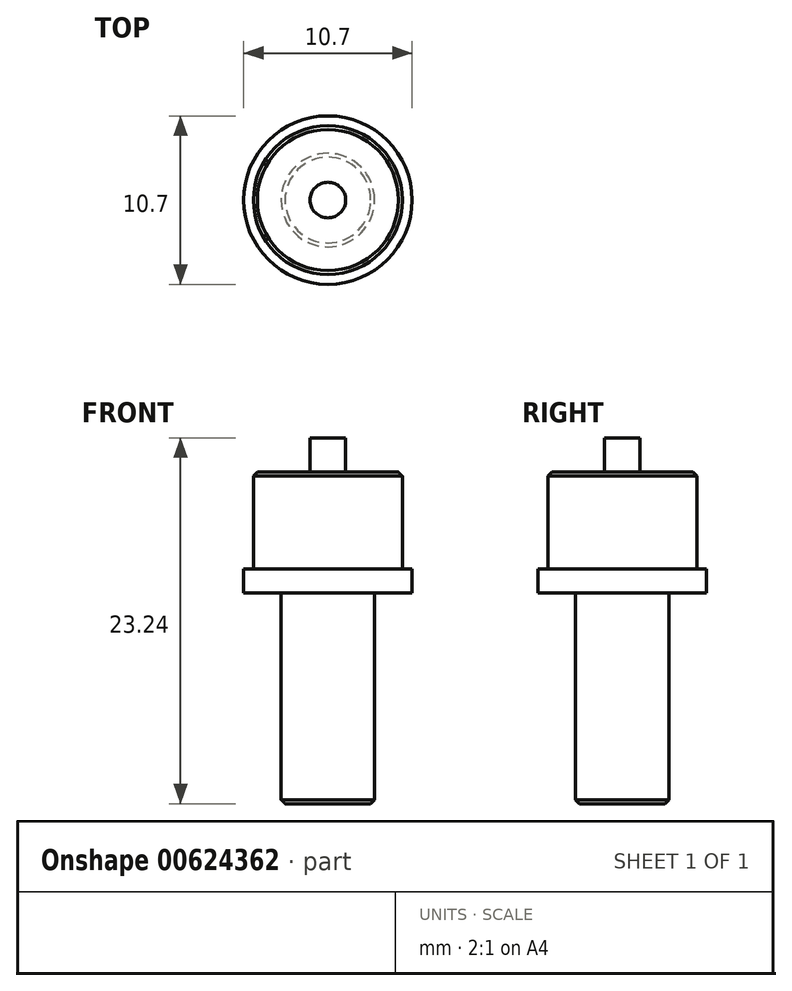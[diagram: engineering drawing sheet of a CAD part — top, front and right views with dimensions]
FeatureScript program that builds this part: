
annotation { "Feature Type Name" : "Feature", "Feature Type Description" : "" }
export const myFeature = defineFeature(function(context is Context, id is Id, definition is map)
    precondition{}
    {
        {
            var Q0;
            Q0=qCreatedBy(makeId("Top.planeOp"),FACE);
            var sketch = newSketch(context, id + "F0", { "sketchPlane" : qUnion([Q0])});
            skCircle(sketch, "E0", {"center": v(0, 0) * mm, "radius": 5.35 * mm});
            skSolve(sketch);
        }
        {
            var Q0;
            Q0=makeQuery(id+"F0.imprint","IMPRINT",FACE,{"disambiguationData":[TD([[makeQuery(id+"F0.imprint","IMPRINT",EDGE,{"derivedFrom":sQuery(id+"F0.wireOp",EDGE,"E0")}),1.0]])]});
            extrude(context, id + "F1", {"entities" : qUnion([Q0]), "depth" : 1.5 * mm, "offsetDistance" : 25 * mm});
        }
        {
            var Q0;
            Q0=makeQuery(id+"F1.opExtrude","CAP_FACE",FACE,{"disambiguationData":[OSD([sQuery(id+"F0.wireOp",EDGE,"E0")])],"isStart":false});
            var sketch = newSketch(context, id + "F2", { "sketchPlane" : qUnion([Q0])});
            skCircle(sketch, "E1", {"center": v(0, 0) * mm, "radius": 4.73 * mm});
            skSolve(sketch);
        }
        {
            var Q0;
            Q0=makeQuery(id+"F2.imprint","IMPRINT",FACE,{"disambiguationData":[TD([[makeQuery(id+"F2.imprint","IMPRINT",EDGE,{"derivedFrom":sQuery(id+"F2.wireOp",EDGE,"E1")}),1.0]])]});
            extrude(context, id + "F3", {"entities" : qUnion([Q0]), "operationType" : NewBodyOperationType.ADD, "depth" : 6.16 * mm, "offsetDistance" : 25 * mm});
        }
        {
            var Q0;
            Q0=makeQuery(id+"F1.opExtrude","CAP_FACE",FACE,{"disambiguationData":[OSD([sQuery(id+"F0.wireOp",EDGE,"E0")])],"isStart":true});
            var sketch = newSketch(context, id + "F4", { "sketchPlane" : qUnion([Q0])});
            skCircle(sketch, "E2", {"center": v(0, 0) * mm, "radius": 2.97 * mm});
            skSolve(sketch);
        }
        {
            var Q0;
            Q0=makeQuery(id+"F4.imprint","IMPRINT",FACE,{"disambiguationData":[TD([[makeQuery(id+"F4.imprint","IMPRINT",EDGE,{"derivedFrom":sQuery(id+"F4.wireOp",EDGE,"E2")}),1.0]])]});
            extrude(context, id + "F5", {"entities" : qUnion([Q0]), "operationType" : NewBodyOperationType.ADD, "depth" : 13.4 * mm, "offsetDistance" : 25 * mm});
        }
        {
            var Q0;
            Q0=makeQuery(id+"F3.opExtrude","CAP_FACE",FACE,{"disambiguationData":[OSD([sQuery(id+"F2.wireOp",EDGE,"E1")])],"isStart":false});
            var sketch = newSketch(context, id + "F6", { "sketchPlane" : qUnion([Q0])});
            skCircle(sketch, "E3", {"center": v(0, 0) * mm, "radius": 1.13 * mm});
            skSolve(sketch);
        }
        {
            var Q0;
            Q0=makeQuery(id+"F6.imprint","IMPRINT",FACE,{"disambiguationData":[TD([[makeQuery(id+"F6.imprint","IMPRINT",EDGE,{"derivedFrom":sQuery(id+"F6.wireOp",EDGE,"E3")}),1.0]])]});
            extrude(context, id + "F7", {"entities" : qUnion([Q0]), "operationType" : NewBodyOperationType.ADD, "depth" : 2.18 * mm, "offsetDistance" : 25 * mm});
        }
        {
            var Q0;
            Q0=makeQuery(id+"F3.opExtrude","CAP_EDGE",EDGE,{"disambiguationData":[OSD([sQuery(id+"F2.wireOp",EDGE,"E1")])],"isStart":false});
            chamfer(context, id + "F8", {"entities" : qUnion([Q0]), "width" : 0.25 * mm, "tangentPropagation" : true});
        }
        {
            var Q0;
            Q0=makeQuery(id+"F5.opExtrude","CAP_EDGE",EDGE,{"disambiguationData":[OSD([sQuery(id+"F4.wireOp",EDGE,"E2")])],"isStart":false});
            chamfer(context, id + "F9", {"entities" : qUnion([Q0]), "width" : 0.25 * mm, "tangentPropagation" : true});
        }
    });
